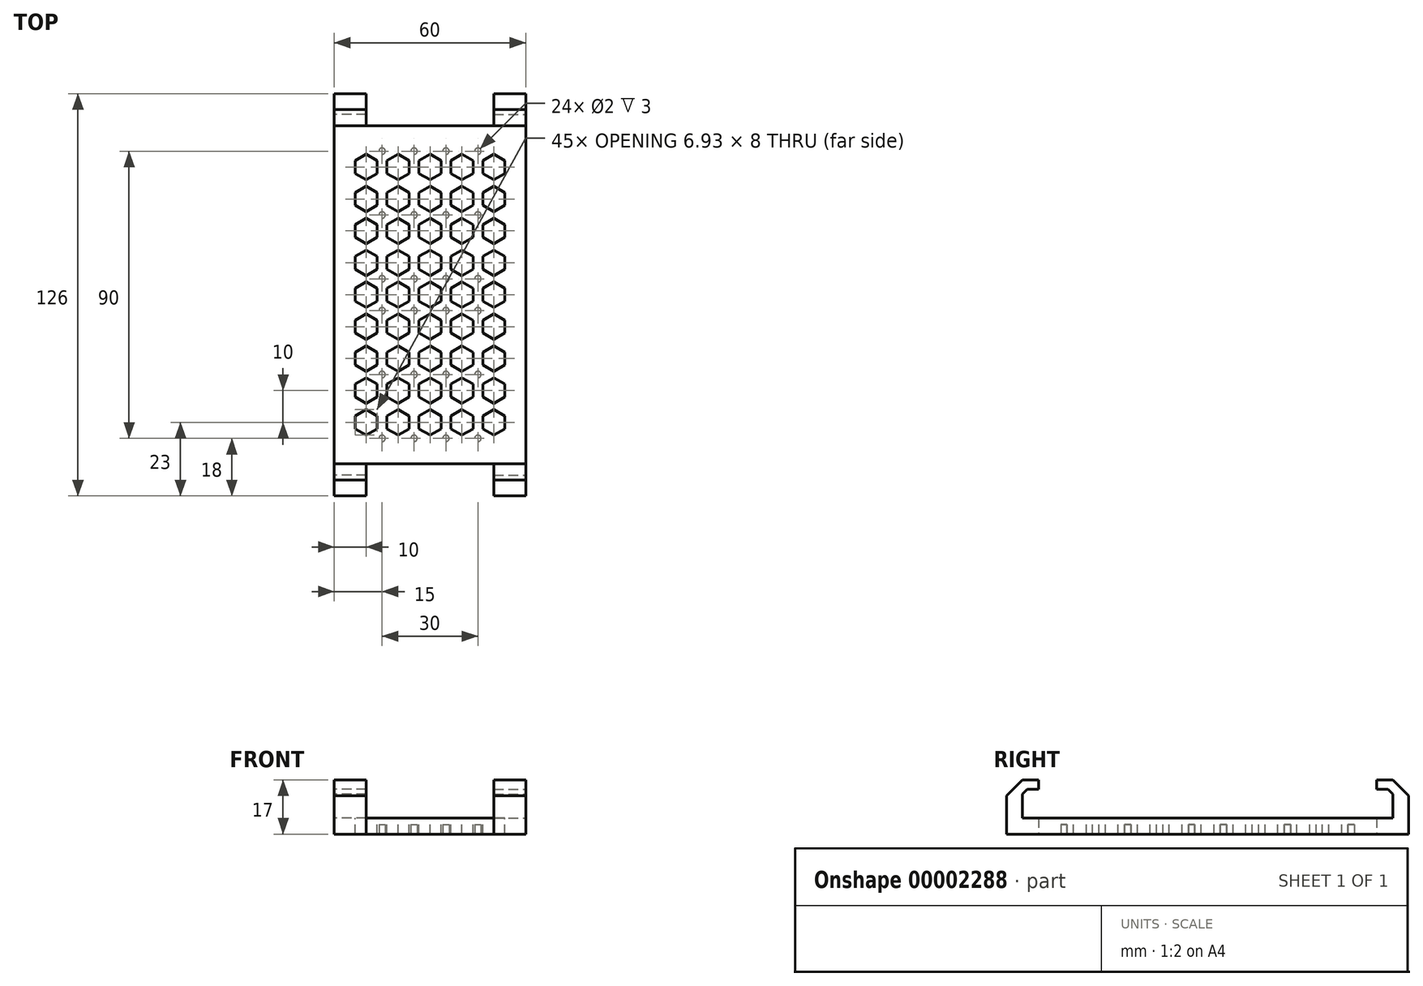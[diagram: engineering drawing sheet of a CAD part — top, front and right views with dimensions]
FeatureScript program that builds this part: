
annotation { "Feature Type Name" : "Feature", "Feature Type Description" : "" }
export const myFeature = defineFeature(function(context is Context, id is Id, definition is map)
    precondition{}
    {
        {
            var Q0;
            Q0=qCreatedBy(makeId("Top.planeOp"),FACE);
            var sketch = newSketch(context, id + "F0", { "sketchPlane" : qUnion([Q0])});
            skPoint(sketch, "E0.rect.middle", {"position": v(0, 0) * mm});
            skLineSegment(sketch, "E1", {"start": v(0, 53) * mm, "end": v(0, 0) * mm, "construction": true});
            skLineSegment(sketch, "E2.bottom", {"start": v(-30, 53) * mm, "end": v(-20, 53) * mm});
            skLineSegment(sketch, "E2.top", {"start": v(-30, 63) * mm, "end": v(-20, 63) * mm});
            skLineSegment(sketch, "E2.left", {"start": v(-30, 53) * mm, "end": v(-30, 63) * mm});
            skLineSegment(sketch, "E2.right", {"start": v(-20, 53) * mm, "end": v(-20, 63) * mm});
            skLineSegment(sketch, "E3", {"start": v(-30, 53) * mm, "end": v(-30, 0) * mm});
            skLineSegment(sketch, "E4", {"start": v(0, 0) * mm, "end": v(0, 53) * mm});
            skLineSegment(sketch, "E5", {"start": v(0, 0) * mm, "end": v(-30, 0) * mm});
            skLineSegment(sketch, "E6", {"start": v(-20, 53) * mm, "end": v(0, 53) * mm});
            skSolve(sketch);
        }
        {
            var Q0;
            Q0=qSketchRegion(id+"F0",true);
            extrude(context, id + "F1", {"entities" : qUnion([Q0]), "depth" : 5 * mm});
        }
        {
            var Q0;
            Q0=makeQuery(id+"F1.opExtrude","CAP_FACE",FACE,{"disambiguationData":[OSD([sQuery(id+"F0.wireOp",EDGE,"E0.rect.bottom"),sQuery(id+"F0.wireOp",EDGE,"E0.rect.left"),sQuery(id+"F0.wireOp",EDGE,"E0.rect.right"),sQuery(id+"F0.wireOp",EDGE,"E2.top"),sQuery(id+"F0.wireOp",EDGE,"E2.left"),sQuery(id+"F0.wireOp",EDGE,"E2.right"),sQuery(id+"F0.wireOp",EDGE,"1c330962-604c-4609-a742-9f983cd8eae2.top"),sQuery(id+"F0.wireOp",EDGE,"1c330962-604c-4609-a742-9f983cd8eae2.right"),sQuery(id+"F0.wireOp",EDGE,"8dd78533-71ad-427a-a356-95920263071d.0.MirrorCS"),sQuery(id+"F0.wireOp",EDGE,"a11a952b-e788-4085-9705-cff0ed95dc66.0.MirrorCS"),sQuery(id+"F0.wireOp",EDGE,"e45f0957-0954-452c-b698-723b5105295b.0.MirrorCS"),sQuery(id+"F0.wireOp",EDGE,"f61b77d5-9dc9-4dc6-a36b-fe702def4f4e.0.MirrorCS"),sQuery(id+"F0.wireOp",EDGE,"6235bd68-9394-4ea3-bb8d-64f7bd4e6ca2.0.MirrorCS"),sQuery(id+"F0.wireOp",EDGE,"5c020b64-50e3-4a5a-bb07-0855aa4a13f5.0.MirrorCS"),sQuery(id+"F0.wireOp",EDGE,"5c020b64-50e3-4a5a-bb07-0855aa4a13f5.1.MirrorCS"),sQuery(id+"F0.wireOp",EDGE,"5c020b64-50e3-4a5a-bb07-0855aa4a13f5.2.MirrorCS"),sQuery(id+"F0.wireOp",EDGE,"5c020b64-50e3-4a5a-bb07-0855aa4a13f5.3.MirrorCS"),sQuery(id+"F0.wireOp",EDGE,"5c020b64-50e3-4a5a-bb07-0855aa4a13f5.4.MirrorCS"),sQuery(id+"F0.wireOp",EDGE,"5c020b64-50e3-4a5a-bb07-0855aa4a13f5.6.MirrorCS"),sQuery(id+"F0.wireOp",EDGE,"5c020b64-50e3-4a5a-bb07-0855aa4a13f5.7.MirrorCS"),sQuery(id+"F0.wireOp",EDGE,"5c020b64-50e3-4a5a-bb07-0855aa4a13f5.9.MirrorCS"),sQuery(id+"F0.wireOp",EDGE,"5c020b64-50e3-4a5a-bb07-0855aa4a13f5.11.MirrorCS"),sQuery(id+"F0.wireOp",EDGE,"5c020b64-50e3-4a5a-bb07-0855aa4a13f5.12.MirrorCS"),sQuery(id+"F0.wireOp",EDGE,"5c020b64-50e3-4a5a-bb07-0855aa4a13f5.13.MirrorCS")])],"isStart":false});
            var sketch = newSketch(context, id + "F2", { "sketchPlane" : qUnion([Q0])});
            skLineSegment(sketch, "E7.bottom", {"start": v(-30, 63) * mm, "end": v(-20, 63) * mm});
            skLineSegment(sketch, "E7.top", {"start": v(-30, 53) * mm, "end": v(-20, 53) * mm});
            skLineSegment(sketch, "E7.left", {"start": v(-30, 63) * mm, "end": v(-30, 53) * mm});
            skLineSegment(sketch, "E7.right", {"start": v(-20, 63) * mm, "end": v(-20, 53) * mm});
            skSolve(sketch);
        }
        {
            var Q0;
            {var subQ3=sQuery(id+"F2.wireOp",EDGE,"E7.bottom");Q0=makeQuery(id+"F2.imprint","IMPRINT",FACE,{"disambiguationData":[TD([[makeQuery(id+"F2.imprint","IMPRINT",EDGE,{"derivedFrom":subQ3}),-1.0]])]});}
            var Q1;
            Q1=makeQuery(id+"F2.imprint","IMPRINT",FACE,{"disambiguationData":[TD([[makeQuery(id+"F2.imprint","IMPRINT",EDGE,{"derivedFrom":sQuery(id+"F2.wireOp",EDGE,"2fed119a-9cd5-4496-afa1-b7d2d9dcd837.bottom")}),1.0]])]});
            extrude(context, id + "F3", {"entities" : qUnion([Q0, Q1]), "operationType" : NewBodyOperationType.ADD, "depth" : 12 * mm});
        }
        {
            var Q0;
            Q0=makeQuery(id+"F3.boolean.opBoolean","MERGE",FACE,{"derivedFrom":[makeQuery(id+"F1.opExtrude","SWEPT_FACE",FACE,{"disambiguationData":[OSD([sQuery(id+"F0.wireOp",EDGE,"E2.left"),sQuery(id+"F0.wireOp",EDGE,"E3")])]}),makeQuery(id+"F3.opExtrude","SWEPT_FACE",FACE,{"disambiguationData":[OSD([sQuery(id+"F2.wireOp",EDGE,"E7.left")])]})]});
            var sketch = newSketch(context, id + "F4", { "sketchPlane" : qUnion([Q0])});
            skLineSegment(sketch, "E8", {"start": v(-63, 17) * mm, "end": v(-58, 17) * mm});
            skLineSegment(sketch, "E9", {"start": v(-58, 17) * mm, "end": v(-63, 12) * mm});
            skLineSegment(sketch, "E10", {"start": v(-63, 12) * mm, "end": v(-63, 17) * mm});
            skSolve(sketch);
        }
        {
            var Q0;
            Q0=qSketchRegion(id+"F4",true);
            extrude(context, id + "F5", {"entities" : qUnion([Q0]), "operationType" : NewBodyOperationType.REMOVE, "endBound" : BoundingType.THROUGH_ALL, "oppositeDirection" : true, "depth" : 25 * mm});
        }
        {
            var Q0;
            Q0=makeQuery(id+"F3.boolean.opBoolean","MERGE",FACE,{"derivedFrom":[makeQuery(id+"F1.opExtrude","SWEPT_FACE",FACE,{"disambiguationData":[OSD([sQuery(id+"F0.wireOp",EDGE,"E2.left"),sQuery(id+"F0.wireOp",EDGE,"E3")])]}),makeQuery(id+"F3.opExtrude","SWEPT_FACE",FACE,{"disambiguationData":[OSD([sQuery(id+"F2.wireOp",EDGE,"E7.left")])]})]});
            var sketch = newSketch(context, id + "F6", { "sketchPlane" : qUnion([Q0])});
            skLineSegment(sketch, "E11", {"start": v(-58, 12.5) * mm, "end": v(-58, 5) * mm});
            skLineSegment(sketch, "E12", {"start": v(-58, 5) * mm, "end": v(-53, 5) * mm});
            skLineSegment(sketch, "E13", {"start": v(-53, 5) * mm, "end": v(-53, 14) * mm});
            skLineSegment(sketch, "E14", {"start": v(-53, 14) * mm, "end": v(-56.5, 14) * mm});
            skLineSegment(sketch, "E15", {"start": v(-56.5, 14) * mm, "end": v(-58, 12.5) * mm});
            skSolve(sketch);
        }
        {
            var Q0;
            Q0=makeQuery(id+"F6.imprint","IMPRINT",FACE,{"disambiguationData":[TD([[makeQuery(id+"F6.imprint","IMPRINT",EDGE,{"derivedFrom":sQuery(id+"F6.wireOp",EDGE,"E11")}),1.0]])]});
            extrude(context, id + "F7", {"entities" : qUnion([Q0]), "operationType" : NewBodyOperationType.REMOVE, "endBound" : BoundingType.THROUGH_ALL, "oppositeDirection" : true, "depth" : 25 * mm});
        }
        {
            var Q0;
            Q0=makeQuery(id+"F1.opExtrude","SWEPT_BODY",BODY,{"disambiguationData":[OSD([sQuery(id+"F0.wireOp",EDGE,"E2.top"),sQuery(id+"F0.wireOp",EDGE,"E2.left"),sQuery(id+"F0.wireOp",EDGE,"E2.right"),sQuery(id+"F0.wireOp",EDGE,"1c330962-604c-4609-a742-9f983cd8eae2.top"),sQuery(id+"F0.wireOp",EDGE,"1c330962-604c-4609-a742-9f983cd8eae2.right"),sQuery(id+"F0.wireOp",EDGE,"5cd1e43b-32d5-4ed1-a398-68d3a370d18f.0.MirrorCS"),sQuery(id+"F0.wireOp",EDGE,"E3"),sQuery(id+"F0.wireOp",EDGE,"E4"),sQuery(id+"F0.wireOp",EDGE,"E5"),sQuery(id+"F0.wireOp",EDGE,"E6")])]});
            var Q1;
            Q1=qCreatedBy(makeId("Right.planeOp"),FACE);
            mirror(context, id + "F8", {"entities" : qUnion([Q0]), "mirrorPlane" : qUnion([Q1])});
        }
        {
            var Q0;
            Q0=makeQuery(id+"F8.opPattern","COPY",BODY,{"derivedFrom":makeQuery(id+"F1.opExtrude","SWEPT_BODY",BODY,{"disambiguationData":[OSD([sQuery(id+"F0.wireOp",EDGE,"E2.top"),sQuery(id+"F0.wireOp",EDGE,"E2.left"),sQuery(id+"F0.wireOp",EDGE,"E2.right"),sQuery(id+"F0.wireOp",EDGE,"1c330962-604c-4609-a742-9f983cd8eae2.top"),sQuery(id+"F0.wireOp",EDGE,"1c330962-604c-4609-a742-9f983cd8eae2.right"),sQuery(id+"F0.wireOp",EDGE,"5cd1e43b-32d5-4ed1-a398-68d3a370d18f.0.MirrorCS"),sQuery(id+"F0.wireOp",EDGE,"E3"),sQuery(id+"F0.wireOp",EDGE,"E4"),sQuery(id+"F0.wireOp",EDGE,"E5"),sQuery(id+"F0.wireOp",EDGE,"E6")])]}),"instanceName":"1"});
            var Q1;
            Q1=makeQuery(id+"F1.opExtrude","SWEPT_BODY",BODY,{"disambiguationData":[OSD([sQuery(id+"F0.wireOp",EDGE,"E2.top"),sQuery(id+"F0.wireOp",EDGE,"E2.left"),sQuery(id+"F0.wireOp",EDGE,"E2.right"),sQuery(id+"F0.wireOp",EDGE,"1c330962-604c-4609-a742-9f983cd8eae2.top"),sQuery(id+"F0.wireOp",EDGE,"1c330962-604c-4609-a742-9f983cd8eae2.right"),sQuery(id+"F0.wireOp",EDGE,"5cd1e43b-32d5-4ed1-a398-68d3a370d18f.0.MirrorCS"),sQuery(id+"F0.wireOp",EDGE,"E3"),sQuery(id+"F0.wireOp",EDGE,"E4"),sQuery(id+"F0.wireOp",EDGE,"E5"),sQuery(id+"F0.wireOp",EDGE,"E6")])]});
            var Q2;
            Q2=qCreatedBy(makeId("Front.planeOp"),FACE);
            mirror(context, id + "F9", {"entities" : qUnion([Q0, Q1]), "mirrorPlane" : qUnion([Q2])});
        }
        {
            var Q0;
            Q0=makeQuery(id+"F1.opExtrude","SWEPT_BODY",BODY,{"disambiguationData":[OSD([sQuery(id+"F0.wireOp",EDGE,"E2.top"),sQuery(id+"F0.wireOp",EDGE,"E2.left"),sQuery(id+"F0.wireOp",EDGE,"E2.right"),sQuery(id+"F0.wireOp",EDGE,"1c330962-604c-4609-a742-9f983cd8eae2.top"),sQuery(id+"F0.wireOp",EDGE,"1c330962-604c-4609-a742-9f983cd8eae2.right"),sQuery(id+"F0.wireOp",EDGE,"5cd1e43b-32d5-4ed1-a398-68d3a370d18f.0.MirrorCS"),sQuery(id+"F0.wireOp",EDGE,"E3"),sQuery(id+"F0.wireOp",EDGE,"E4"),sQuery(id+"F0.wireOp",EDGE,"E5"),sQuery(id+"F0.wireOp",EDGE,"E6")])]});
            var Q1;
            Q1=makeQuery(id+"F8.opPattern","COPY",BODY,{"derivedFrom":makeQuery(id+"F1.opExtrude","SWEPT_BODY",BODY,{"disambiguationData":[OSD([sQuery(id+"F0.wireOp",EDGE,"E2.top"),sQuery(id+"F0.wireOp",EDGE,"E2.left"),sQuery(id+"F0.wireOp",EDGE,"E2.right"),sQuery(id+"F0.wireOp",EDGE,"1c330962-604c-4609-a742-9f983cd8eae2.top"),sQuery(id+"F0.wireOp",EDGE,"1c330962-604c-4609-a742-9f983cd8eae2.right"),sQuery(id+"F0.wireOp",EDGE,"5cd1e43b-32d5-4ed1-a398-68d3a370d18f.0.MirrorCS"),sQuery(id+"F0.wireOp",EDGE,"E3"),sQuery(id+"F0.wireOp",EDGE,"E4"),sQuery(id+"F0.wireOp",EDGE,"E5"),sQuery(id+"F0.wireOp",EDGE,"E6")])]}),"instanceName":"1"});
            var Q2;
            Q2=makeQuery(id+"F9.opPattern","COPY",BODY,{"derivedFrom":makeQuery(id+"F1.opExtrude","SWEPT_BODY",BODY,{"disambiguationData":[OSD([sQuery(id+"F0.wireOp",EDGE,"E2.top"),sQuery(id+"F0.wireOp",EDGE,"E2.left"),sQuery(id+"F0.wireOp",EDGE,"E2.right"),sQuery(id+"F0.wireOp",EDGE,"1c330962-604c-4609-a742-9f983cd8eae2.top"),sQuery(id+"F0.wireOp",EDGE,"1c330962-604c-4609-a742-9f983cd8eae2.right"),sQuery(id+"F0.wireOp",EDGE,"5cd1e43b-32d5-4ed1-a398-68d3a370d18f.0.MirrorCS"),sQuery(id+"F0.wireOp",EDGE,"E3"),sQuery(id+"F0.wireOp",EDGE,"E4"),sQuery(id+"F0.wireOp",EDGE,"E5"),sQuery(id+"F0.wireOp",EDGE,"E6")])]}),"instanceName":"1"});
            var Q3;
            Q3=makeQuery(id+"F9.opPattern","COPY",BODY,{"derivedFrom":makeQuery(id+"F8.opPattern","COPY",BODY,{"derivedFrom":makeQuery(id+"F1.opExtrude","SWEPT_BODY",BODY,{"disambiguationData":[OSD([sQuery(id+"F0.wireOp",EDGE,"E2.top"),sQuery(id+"F0.wireOp",EDGE,"E2.left"),sQuery(id+"F0.wireOp",EDGE,"E2.right"),sQuery(id+"F0.wireOp",EDGE,"1c330962-604c-4609-a742-9f983cd8eae2.top"),sQuery(id+"F0.wireOp",EDGE,"1c330962-604c-4609-a742-9f983cd8eae2.right"),sQuery(id+"F0.wireOp",EDGE,"5cd1e43b-32d5-4ed1-a398-68d3a370d18f.0.MirrorCS"),sQuery(id+"F0.wireOp",EDGE,"E3"),sQuery(id+"F0.wireOp",EDGE,"E4"),sQuery(id+"F0.wireOp",EDGE,"E5"),sQuery(id+"F0.wireOp",EDGE,"E6")])]}),"instanceName":"1"}),"instanceName":"1"});
            booleanBodies(context, id + "F10", {"operationType" : BooleanOperationType.UNION, "tools" : qUnion([Q0, Q1, Q2, Q3])});
        }
        {
            var Q0;
            {var subQ0=sQuery(id+"F0.wireOp",EDGE,"E2.left");var subQ1=sQuery(id+"F0.wireOp",EDGE,"E2.right");var subQ2=sQuery(id+"F0.wireOp",EDGE,"5cd1e43b-32d5-4ed1-a398-68d3a370d18f.0.MirrorCS");var subQ3=sQuery(id+"F0.wireOp",EDGE,"E3");var subQ4=sQuery(id+"F0.wireOp",EDGE,"E4");var subQ5=sQuery(id+"F0.wireOp",EDGE,"E5");var subQ6=sQuery(id+"F0.wireOp",EDGE,"E6");var subQ7=makeQuery(id+"Fhmo5EDbbS1xftA_1.boolean.opBoolean","SPLIT",FACE,{"disambiguationData":[TD([makeQuery(id+"F1.opExtrude","SWEPT_FACE",FACE,{"disambiguationData":[OSD([subQ1])]})])],"derivedFrom":makeQuery(id+"F1.opExtrude","CAP_FACE",FACE,{"disambiguationData":[OSD([sQuery(id+"F0.wireOp",EDGE,"E2.top"),subQ0,subQ1,sQuery(id+"F0.wireOp",EDGE,"1c330962-604c-4609-a742-9f983cd8eae2.top"),sQuery(id+"F0.wireOp",EDGE,"1c330962-604c-4609-a742-9f983cd8eae2.right"),subQ2,subQ3,subQ4,subQ5,subQ6])],"isStart":false})});var subQ8=makeQuery(id+"F8.opPattern","COPY",FACE,{"derivedFrom":subQ7,"instanceName":"1"});Q0=makeQuery(id+"F10.opBoolean","MERGE",FACE,{"derivedFrom":[subQ7,subQ8,makeQuery(id+"F9.opPattern","COPY",FACE,{"derivedFrom":subQ7,"instanceName":"1"}),makeQuery(id+"F9.opPattern","COPY",FACE,{"derivedFrom":subQ8,"instanceName":"1"})]});}
            var sketch = newSketch(context, id + "F11", { "sketchPlane" : qUnion([Q0])});
            skCircle(sketch, "E16.cCircle", {"center": v(-20, 40) * mm, "radius": 4 * mm, "construction": true});
            skLineSegment(sketch, "E16.0", {"start": v(-16.54, 38) * mm, "end": v(-20, 36) * mm});
            skLineSegment(sketch, "E16.1", {"start": v(-20, 36) * mm, "end": v(-23.46, 38) * mm});
            skLineSegment(sketch, "E16.2", {"start": v(-23.46, 38) * mm, "end": v(-23.46, 42) * mm});
            skLineSegment(sketch, "E16.3", {"start": v(-23.46, 42) * mm, "end": v(-20, 44) * mm});
            skLineSegment(sketch, "E16.4", {"start": v(-20, 44) * mm, "end": v(-16.54, 42) * mm});
            skLineSegment(sketch, "E16.5", {"start": v(-16.54, 42) * mm, "end": v(-16.54, 38) * mm});
            skLineSegment(sketch, "E17.0.1.0", {"start": v(-23.46, 28) * mm, "end": v(-23.46, 32) * mm});
            skLineSegment(sketch, "E17.0.1.1", {"start": v(-23.46, 32) * mm, "end": v(-20, 34) * mm});
            skLineSegment(sketch, "E17.0.1.2", {"start": v(-20, 34) * mm, "end": v(-16.54, 32) * mm});
            skLineSegment(sketch, "E17.0.1.3", {"start": v(-16.54, 32) * mm, "end": v(-16.54, 28) * mm});
            skLineSegment(sketch, "E17.0.1.4", {"start": v(-16.54, 28) * mm, "end": v(-20, 26) * mm});
            skLineSegment(sketch, "E17.0.1.5", {"start": v(-20, 26) * mm, "end": v(-23.46, 28) * mm});
            skLineSegment(sketch, "E17.0.2.0", {"start": v(-23.46, 18) * mm, "end": v(-23.46, 22) * mm});
            skLineSegment(sketch, "E17.0.2.1", {"start": v(-23.46, 22) * mm, "end": v(-20, 24) * mm});
            skLineSegment(sketch, "E17.0.2.2", {"start": v(-20, 24) * mm, "end": v(-16.54, 22) * mm});
            skLineSegment(sketch, "E17.0.2.3", {"start": v(-16.54, 22) * mm, "end": v(-16.54, 18) * mm});
            skLineSegment(sketch, "E17.0.2.4", {"start": v(-16.54, 18) * mm, "end": v(-20, 16) * mm});
            skLineSegment(sketch, "E17.0.2.5", {"start": v(-20, 16) * mm, "end": v(-23.46, 18) * mm});
            skLineSegment(sketch, "E17.0.3.0", {"start": v(-23.46, 8) * mm, "end": v(-23.46, 12) * mm});
            skLineSegment(sketch, "E17.0.3.1", {"start": v(-23.46, 12) * mm, "end": v(-20, 14) * mm});
            skLineSegment(sketch, "E17.0.3.2", {"start": v(-20, 14) * mm, "end": v(-16.54, 12) * mm});
            skLineSegment(sketch, "E17.0.3.3", {"start": v(-16.54, 12) * mm, "end": v(-16.54, 8) * mm});
            skLineSegment(sketch, "E17.0.3.4", {"start": v(-16.54, 8) * mm, "end": v(-20, 6) * mm});
            skLineSegment(sketch, "E17.0.3.5", {"start": v(-20, 6) * mm, "end": v(-23.46, 8) * mm});
            skLineSegment(sketch, "E17.0.4.0", {"start": v(-23.46, -2) * mm, "end": v(-23.46, 2) * mm});
            skLineSegment(sketch, "E17.0.4.1", {"start": v(-23.46, 2) * mm, "end": v(-20, 4) * mm});
            skLineSegment(sketch, "E17.0.4.2", {"start": v(-20, 4) * mm, "end": v(-16.54, 2) * mm});
            skLineSegment(sketch, "E17.0.4.3", {"start": v(-16.54, 2) * mm, "end": v(-16.54, -2) * mm});
            skLineSegment(sketch, "E17.0.4.4", {"start": v(-16.54, -2) * mm, "end": v(-20, -4) * mm});
            skLineSegment(sketch, "E17.0.4.5", {"start": v(-20, -4) * mm, "end": v(-23.46, -2) * mm});
            skLineSegment(sketch, "E17.0.5.0", {"start": v(-23.46, -12) * mm, "end": v(-23.46, -8) * mm});
            skLineSegment(sketch, "E17.0.5.1", {"start": v(-23.46, -8) * mm, "end": v(-20, -6) * mm});
            skLineSegment(sketch, "E17.0.5.2", {"start": v(-20, -6) * mm, "end": v(-16.54, -8) * mm});
            skLineSegment(sketch, "E17.0.5.3", {"start": v(-16.54, -8) * mm, "end": v(-16.54, -12) * mm});
            skLineSegment(sketch, "E17.0.5.4", {"start": v(-16.54, -12) * mm, "end": v(-20, -14) * mm});
            skLineSegment(sketch, "E17.0.5.5", {"start": v(-20, -14) * mm, "end": v(-23.46, -12) * mm});
            skLineSegment(sketch, "E17.0.6.0", {"start": v(-23.46, -22) * mm, "end": v(-23.46, -18) * mm});
            skLineSegment(sketch, "E17.0.6.1", {"start": v(-23.46, -18) * mm, "end": v(-20, -16) * mm});
            skLineSegment(sketch, "E17.0.6.2", {"start": v(-20, -16) * mm, "end": v(-16.54, -18) * mm});
            skLineSegment(sketch, "E17.0.6.3", {"start": v(-16.54, -18) * mm, "end": v(-16.54, -22) * mm});
            skLineSegment(sketch, "E17.0.6.4", {"start": v(-16.54, -22) * mm, "end": v(-20, -24) * mm});
            skLineSegment(sketch, "E17.0.6.5", {"start": v(-20, -24) * mm, "end": v(-23.46, -22) * mm});
            skLineSegment(sketch, "E17.0.7.0", {"start": v(-23.46, -32) * mm, "end": v(-23.46, -28) * mm});
            skLineSegment(sketch, "E17.0.7.1", {"start": v(-23.46, -28) * mm, "end": v(-20, -26) * mm});
            skLineSegment(sketch, "E17.0.7.2", {"start": v(-20, -26) * mm, "end": v(-16.54, -28) * mm});
            skLineSegment(sketch, "E17.0.7.3", {"start": v(-16.54, -28) * mm, "end": v(-16.54, -32) * mm});
            skLineSegment(sketch, "E17.0.7.4", {"start": v(-16.54, -32) * mm, "end": v(-20, -34) * mm});
            skLineSegment(sketch, "E17.0.7.5", {"start": v(-20, -34) * mm, "end": v(-23.46, -32) * mm});
            skLineSegment(sketch, "E17.0.8.0", {"start": v(-23.46, -42) * mm, "end": v(-23.46, -38) * mm});
            skLineSegment(sketch, "E17.0.8.1", {"start": v(-23.46, -38) * mm, "end": v(-20, -36) * mm});
            skLineSegment(sketch, "E17.0.8.2", {"start": v(-20, -36) * mm, "end": v(-16.54, -38) * mm});
            skLineSegment(sketch, "E17.0.8.3", {"start": v(-16.54, -38) * mm, "end": v(-16.54, -42) * mm});
            skLineSegment(sketch, "E17.0.8.4", {"start": v(-16.54, -42) * mm, "end": v(-20, -44) * mm});
            skLineSegment(sketch, "E17.0.8.5", {"start": v(-20, -44) * mm, "end": v(-23.46, -42) * mm});
            skLineSegment(sketch, "E17.1.0.0", {"start": v(-13.46, 38) * mm, "end": v(-13.46, 42) * mm});
            skLineSegment(sketch, "E17.1.0.1", {"start": v(-13.46, 42) * mm, "end": v(-10, 44) * mm});
            skLineSegment(sketch, "E17.1.0.2", {"start": v(-10, 44) * mm, "end": v(-6.54, 42) * mm});
            skLineSegment(sketch, "E17.1.0.3", {"start": v(-6.54, 42) * mm, "end": v(-6.54, 38) * mm});
            skLineSegment(sketch, "E17.1.0.4", {"start": v(-6.54, 38) * mm, "end": v(-10, 36) * mm});
            skLineSegment(sketch, "E17.1.0.5", {"start": v(-10, 36) * mm, "end": v(-13.46, 38) * mm});
            skLineSegment(sketch, "E17.1.1.0", {"start": v(-13.46, 28) * mm, "end": v(-13.46, 32) * mm});
            skLineSegment(sketch, "E17.1.1.1", {"start": v(-13.46, 32) * mm, "end": v(-10, 34) * mm});
            skLineSegment(sketch, "E17.1.1.2", {"start": v(-10, 34) * mm, "end": v(-6.54, 32) * mm});
            skLineSegment(sketch, "E17.1.1.3", {"start": v(-6.54, 32) * mm, "end": v(-6.54, 28) * mm});
            skLineSegment(sketch, "E17.1.1.4", {"start": v(-6.54, 28) * mm, "end": v(-10, 26) * mm});
            skLineSegment(sketch, "E17.1.1.5", {"start": v(-10, 26) * mm, "end": v(-13.46, 28) * mm});
            skLineSegment(sketch, "E17.1.2.0", {"start": v(-13.46, 18) * mm, "end": v(-13.46, 22) * mm});
            skLineSegment(sketch, "E17.1.2.1", {"start": v(-13.46, 22) * mm, "end": v(-10, 24) * mm});
            skLineSegment(sketch, "E17.1.2.2", {"start": v(-10, 24) * mm, "end": v(-6.54, 22) * mm});
            skLineSegment(sketch, "E17.1.2.3", {"start": v(-6.54, 22) * mm, "end": v(-6.54, 18) * mm});
            skLineSegment(sketch, "E17.1.2.4", {"start": v(-6.54, 18) * mm, "end": v(-10, 16) * mm});
            skLineSegment(sketch, "E17.1.2.5", {"start": v(-10, 16) * mm, "end": v(-13.46, 18) * mm});
            skLineSegment(sketch, "E17.1.3.0", {"start": v(-13.46, 8) * mm, "end": v(-13.46, 12) * mm});
            skLineSegment(sketch, "E17.1.3.1", {"start": v(-13.46, 12) * mm, "end": v(-10, 14) * mm});
            skLineSegment(sketch, "E17.1.3.2", {"start": v(-10, 14) * mm, "end": v(-6.54, 12) * mm});
            skLineSegment(sketch, "E17.1.3.3", {"start": v(-6.54, 12) * mm, "end": v(-6.54, 8) * mm});
            skLineSegment(sketch, "E17.1.3.4", {"start": v(-6.54, 8) * mm, "end": v(-10, 6) * mm});
            skLineSegment(sketch, "E17.1.3.5", {"start": v(-10, 6) * mm, "end": v(-13.46, 8) * mm});
            skLineSegment(sketch, "E17.1.4.0", {"start": v(-13.46, -2) * mm, "end": v(-13.46, 2) * mm});
            skLineSegment(sketch, "E17.1.4.1", {"start": v(-13.46, 2) * mm, "end": v(-10, 4) * mm});
            skLineSegment(sketch, "E17.1.4.2", {"start": v(-10, 4) * mm, "end": v(-6.54, 2) * mm});
            skLineSegment(sketch, "E17.1.4.3", {"start": v(-6.54, 2) * mm, "end": v(-6.54, -2) * mm});
            skLineSegment(sketch, "E17.1.4.4", {"start": v(-6.54, -2) * mm, "end": v(-10, -4) * mm});
            skLineSegment(sketch, "E17.1.4.5", {"start": v(-10, -4) * mm, "end": v(-13.46, -2) * mm});
            skLineSegment(sketch, "E17.1.5.0", {"start": v(-13.46, -12) * mm, "end": v(-13.46, -8) * mm});
            skLineSegment(sketch, "E17.1.5.1", {"start": v(-13.46, -8) * mm, "end": v(-10, -6) * mm});
            skLineSegment(sketch, "E17.1.5.2", {"start": v(-10, -6) * mm, "end": v(-6.54, -8) * mm});
            skLineSegment(sketch, "E17.1.5.3", {"start": v(-6.54, -8) * mm, "end": v(-6.54, -12) * mm});
            skLineSegment(sketch, "E17.1.5.4", {"start": v(-6.54, -12) * mm, "end": v(-10, -14) * mm});
            skLineSegment(sketch, "E17.1.5.5", {"start": v(-10, -14) * mm, "end": v(-13.46, -12) * mm});
            skLineSegment(sketch, "E17.1.6.0", {"start": v(-13.46, -22) * mm, "end": v(-13.46, -18) * mm});
            skLineSegment(sketch, "E17.1.6.1", {"start": v(-13.46, -18) * mm, "end": v(-10, -16) * mm});
            skLineSegment(sketch, "E17.1.6.2", {"start": v(-10, -16) * mm, "end": v(-6.54, -18) * mm});
            skLineSegment(sketch, "E17.1.6.3", {"start": v(-6.54, -18) * mm, "end": v(-6.54, -22) * mm});
            skLineSegment(sketch, "E17.1.6.4", {"start": v(-6.54, -22) * mm, "end": v(-10, -24) * mm});
            skLineSegment(sketch, "E17.1.6.5", {"start": v(-10, -24) * mm, "end": v(-13.46, -22) * mm});
            skLineSegment(sketch, "E17.1.7.0", {"start": v(-13.46, -32) * mm, "end": v(-13.46, -28) * mm});
            skLineSegment(sketch, "E17.1.7.1", {"start": v(-13.46, -28) * mm, "end": v(-10, -26) * mm});
            skLineSegment(sketch, "E17.1.7.2", {"start": v(-10, -26) * mm, "end": v(-6.54, -28) * mm});
            skLineSegment(sketch, "E17.1.7.3", {"start": v(-6.54, -28) * mm, "end": v(-6.54, -32) * mm});
            skLineSegment(sketch, "E17.1.7.4", {"start": v(-6.54, -32) * mm, "end": v(-10, -34) * mm});
            skLineSegment(sketch, "E17.1.7.5", {"start": v(-10, -34) * mm, "end": v(-13.46, -32) * mm});
            skLineSegment(sketch, "E17.1.8.0", {"start": v(-13.46, -42) * mm, "end": v(-13.46, -38) * mm});
            skLineSegment(sketch, "E17.1.8.1", {"start": v(-13.46, -38) * mm, "end": v(-10, -36) * mm});
            skLineSegment(sketch, "E17.1.8.2", {"start": v(-10, -36) * mm, "end": v(-6.54, -38) * mm});
            skLineSegment(sketch, "E17.1.8.3", {"start": v(-6.54, -38) * mm, "end": v(-6.54, -42) * mm});
            skLineSegment(sketch, "E17.1.8.4", {"start": v(-6.54, -42) * mm, "end": v(-10, -44) * mm});
            skLineSegment(sketch, "E17.1.8.5", {"start": v(-10, -44) * mm, "end": v(-13.46, -42) * mm});
            skLineSegment(sketch, "E17.2.0.0", {"start": v(-3.46, 38) * mm, "end": v(-3.46, 42) * mm});
            skLineSegment(sketch, "E17.2.0.1", {"start": v(-3.46, 42) * mm, "end": v(0, 44) * mm});
            skLineSegment(sketch, "E17.2.0.2", {"start": v(0, 44) * mm, "end": v(3.46, 42) * mm});
            skLineSegment(sketch, "E17.2.0.3", {"start": v(3.46, 42) * mm, "end": v(3.46, 38) * mm});
            skLineSegment(sketch, "E17.2.0.4", {"start": v(3.46, 38) * mm, "end": v(0, 36) * mm});
            skLineSegment(sketch, "E17.2.0.5", {"start": v(0, 36) * mm, "end": v(-3.46, 38) * mm});
            skLineSegment(sketch, "E17.2.1.0", {"start": v(-3.46, 28) * mm, "end": v(-3.46, 32) * mm});
            skLineSegment(sketch, "E17.2.1.1", {"start": v(-3.46, 32) * mm, "end": v(0, 34) * mm});
            skLineSegment(sketch, "E17.2.1.2", {"start": v(0, 34) * mm, "end": v(3.46, 32) * mm});
            skLineSegment(sketch, "E17.2.1.3", {"start": v(3.46, 32) * mm, "end": v(3.46, 28) * mm});
            skLineSegment(sketch, "E17.2.1.4", {"start": v(3.46, 28) * mm, "end": v(0, 26) * mm});
            skLineSegment(sketch, "E17.2.1.5", {"start": v(0, 26) * mm, "end": v(-3.46, 28) * mm});
            skLineSegment(sketch, "E17.2.2.0", {"start": v(-3.46, 18) * mm, "end": v(-3.46, 22) * mm});
            skLineSegment(sketch, "E17.2.2.1", {"start": v(-3.46, 22) * mm, "end": v(0, 24) * mm});
            skLineSegment(sketch, "E17.2.2.2", {"start": v(0, 24) * mm, "end": v(3.46, 22) * mm});
            skLineSegment(sketch, "E17.2.2.3", {"start": v(3.46, 22) * mm, "end": v(3.46, 18) * mm});
            skLineSegment(sketch, "E17.2.2.4", {"start": v(3.46, 18) * mm, "end": v(0, 16) * mm});
            skLineSegment(sketch, "E17.2.2.5", {"start": v(0, 16) * mm, "end": v(-3.46, 18) * mm});
            skLineSegment(sketch, "E17.2.3.0", {"start": v(-3.46, 8) * mm, "end": v(-3.46, 12) * mm});
            skLineSegment(sketch, "E17.2.3.1", {"start": v(-3.46, 12) * mm, "end": v(0, 14) * mm});
            skLineSegment(sketch, "E17.2.3.2", {"start": v(0, 14) * mm, "end": v(3.46, 12) * mm});
            skLineSegment(sketch, "E17.2.3.3", {"start": v(3.46, 12) * mm, "end": v(3.46, 8) * mm});
            skLineSegment(sketch, "E17.2.3.4", {"start": v(3.46, 8) * mm, "end": v(0, 6) * mm});
            skLineSegment(sketch, "E17.2.3.5", {"start": v(0, 6) * mm, "end": v(-3.46, 8) * mm});
            skLineSegment(sketch, "E17.2.4.0", {"start": v(-3.46, -2) * mm, "end": v(-3.46, 2) * mm});
            skLineSegment(sketch, "E17.2.4.1", {"start": v(-3.46, 2) * mm, "end": v(0, 4) * mm});
            skLineSegment(sketch, "E17.2.4.2", {"start": v(0, 4) * mm, "end": v(3.46, 2) * mm});
            skLineSegment(sketch, "E17.2.4.3", {"start": v(3.46, 2) * mm, "end": v(3.46, -2) * mm});
            skLineSegment(sketch, "E17.2.4.4", {"start": v(3.46, -2) * mm, "end": v(0, -4) * mm});
            skLineSegment(sketch, "E17.2.4.5", {"start": v(0, -4) * mm, "end": v(-3.46, -2) * mm});
            skLineSegment(sketch, "E17.2.5.0", {"start": v(-3.46, -12) * mm, "end": v(-3.46, -8) * mm});
            skLineSegment(sketch, "E17.2.5.1", {"start": v(-3.46, -8) * mm, "end": v(0, -6) * mm});
            skLineSegment(sketch, "E17.2.5.2", {"start": v(0, -6) * mm, "end": v(3.46, -8) * mm});
            skLineSegment(sketch, "E17.2.5.3", {"start": v(3.46, -8) * mm, "end": v(3.46, -12) * mm});
            skLineSegment(sketch, "E17.2.5.4", {"start": v(3.46, -12) * mm, "end": v(0, -14) * mm});
            skLineSegment(sketch, "E17.2.5.5", {"start": v(0, -14) * mm, "end": v(-3.46, -12) * mm});
            skLineSegment(sketch, "E17.2.6.0", {"start": v(-3.46, -22) * mm, "end": v(-3.46, -18) * mm});
            skLineSegment(sketch, "E17.2.6.1", {"start": v(-3.46, -18) * mm, "end": v(0, -16) * mm});
            skLineSegment(sketch, "E17.2.6.2", {"start": v(0, -16) * mm, "end": v(3.46, -18) * mm});
            skLineSegment(sketch, "E17.2.6.3", {"start": v(3.46, -18) * mm, "end": v(3.46, -22) * mm});
            skLineSegment(sketch, "E17.2.6.4", {"start": v(3.46, -22) * mm, "end": v(0, -24) * mm});
            skLineSegment(sketch, "E17.2.6.5", {"start": v(0, -24) * mm, "end": v(-3.46, -22) * mm});
            skLineSegment(sketch, "E17.2.7.0", {"start": v(-3.46, -32) * mm, "end": v(-3.46, -28) * mm});
            skLineSegment(sketch, "E17.2.7.1", {"start": v(-3.46, -28) * mm, "end": v(0, -26) * mm});
            skLineSegment(sketch, "E17.2.7.2", {"start": v(0, -26) * mm, "end": v(3.46, -28) * mm});
            skLineSegment(sketch, "E17.2.7.3", {"start": v(3.46, -28) * mm, "end": v(3.46, -32) * mm});
            skLineSegment(sketch, "E17.2.7.4", {"start": v(3.46, -32) * mm, "end": v(0, -34) * mm});
            skLineSegment(sketch, "E17.2.7.5", {"start": v(0, -34) * mm, "end": v(-3.46, -32) * mm});
            skLineSegment(sketch, "E17.2.8.0", {"start": v(-3.46, -42) * mm, "end": v(-3.46, -38) * mm});
            skLineSegment(sketch, "E17.2.8.1", {"start": v(-3.46, -38) * mm, "end": v(0, -36) * mm});
            skLineSegment(sketch, "E17.2.8.2", {"start": v(0, -36) * mm, "end": v(3.46, -38) * mm});
            skLineSegment(sketch, "E17.2.8.3", {"start": v(3.46, -38) * mm, "end": v(3.46, -42) * mm});
            skLineSegment(sketch, "E17.2.8.4", {"start": v(3.46, -42) * mm, "end": v(0, -44) * mm});
            skLineSegment(sketch, "E17.2.8.5", {"start": v(0, -44) * mm, "end": v(-3.46, -42) * mm});
            skLineSegment(sketch, "E17.3.0.0", {"start": v(6.54, 38) * mm, "end": v(6.54, 42) * mm});
            skLineSegment(sketch, "E17.3.0.1", {"start": v(6.54, 42) * mm, "end": v(10, 44) * mm});
            skLineSegment(sketch, "E17.3.0.2", {"start": v(10, 44) * mm, "end": v(13.46, 42) * mm});
            skLineSegment(sketch, "E17.3.0.3", {"start": v(13.46, 42) * mm, "end": v(13.46, 38) * mm});
            skLineSegment(sketch, "E17.3.0.4", {"start": v(13.46, 38) * mm, "end": v(10, 36) * mm});
            skLineSegment(sketch, "E17.3.0.5", {"start": v(10, 36) * mm, "end": v(6.54, 38) * mm});
            skLineSegment(sketch, "E17.3.1.0", {"start": v(6.54, 28) * mm, "end": v(6.54, 32) * mm});
            skLineSegment(sketch, "E17.3.1.1", {"start": v(6.54, 32) * mm, "end": v(10, 34) * mm});
            skLineSegment(sketch, "E17.3.1.2", {"start": v(10, 34) * mm, "end": v(13.46, 32) * mm});
            skLineSegment(sketch, "E17.3.1.3", {"start": v(13.46, 32) * mm, "end": v(13.46, 28) * mm});
            skLineSegment(sketch, "E17.3.1.4", {"start": v(13.46, 28) * mm, "end": v(10, 26) * mm});
            skLineSegment(sketch, "E17.3.1.5", {"start": v(10, 26) * mm, "end": v(6.54, 28) * mm});
            skLineSegment(sketch, "E17.3.2.0", {"start": v(6.54, 18) * mm, "end": v(6.54, 22) * mm});
            skLineSegment(sketch, "E17.3.2.1", {"start": v(6.54, 22) * mm, "end": v(10, 24) * mm});
            skLineSegment(sketch, "E17.3.2.2", {"start": v(10, 24) * mm, "end": v(13.46, 22) * mm});
            skLineSegment(sketch, "E17.3.2.3", {"start": v(13.46, 22) * mm, "end": v(13.46, 18) * mm});
            skLineSegment(sketch, "E17.3.2.4", {"start": v(13.46, 18) * mm, "end": v(10, 16) * mm});
            skLineSegment(sketch, "E17.3.2.5", {"start": v(10, 16) * mm, "end": v(6.54, 18) * mm});
            skLineSegment(sketch, "E17.3.3.0", {"start": v(6.54, 8) * mm, "end": v(6.54, 12) * mm});
            skLineSegment(sketch, "E17.3.3.1", {"start": v(6.54, 12) * mm, "end": v(10, 14) * mm});
            skLineSegment(sketch, "E17.3.3.2", {"start": v(10, 14) * mm, "end": v(13.46, 12) * mm});
            skLineSegment(sketch, "E17.3.3.3", {"start": v(13.46, 12) * mm, "end": v(13.46, 8) * mm});
            skLineSegment(sketch, "E17.3.3.4", {"start": v(13.46, 8) * mm, "end": v(10, 6) * mm});
            skLineSegment(sketch, "E17.3.3.5", {"start": v(10, 6) * mm, "end": v(6.54, 8) * mm});
            skLineSegment(sketch, "E17.3.4.0", {"start": v(6.54, -2) * mm, "end": v(6.54, 2) * mm});
            skLineSegment(sketch, "E17.3.4.1", {"start": v(6.54, 2) * mm, "end": v(10, 4) * mm});
            skLineSegment(sketch, "E17.3.4.2", {"start": v(10, 4) * mm, "end": v(13.46, 2) * mm});
            skLineSegment(sketch, "E17.3.4.3", {"start": v(13.46, 2) * mm, "end": v(13.46, -2) * mm});
            skLineSegment(sketch, "E17.3.4.4", {"start": v(13.46, -2) * mm, "end": v(10, -4) * mm});
            skLineSegment(sketch, "E17.3.4.5", {"start": v(10, -4) * mm, "end": v(6.54, -2) * mm});
            skLineSegment(sketch, "E17.3.5.0", {"start": v(6.54, -12) * mm, "end": v(6.54, -8) * mm});
            skLineSegment(sketch, "E17.3.5.1", {"start": v(6.54, -8) * mm, "end": v(10, -6) * mm});
            skLineSegment(sketch, "E17.3.5.2", {"start": v(10, -6) * mm, "end": v(13.46, -8) * mm});
            skLineSegment(sketch, "E17.3.5.3", {"start": v(13.46, -8) * mm, "end": v(13.46, -12) * mm});
            skLineSegment(sketch, "E17.3.5.4", {"start": v(13.46, -12) * mm, "end": v(10, -14) * mm});
            skLineSegment(sketch, "E17.3.5.5", {"start": v(10, -14) * mm, "end": v(6.54, -12) * mm});
            skLineSegment(sketch, "E17.3.6.0", {"start": v(6.54, -22) * mm, "end": v(6.54, -18) * mm});
            skLineSegment(sketch, "E17.3.6.1", {"start": v(6.54, -18) * mm, "end": v(10, -16) * mm});
            skLineSegment(sketch, "E17.3.6.2", {"start": v(10, -16) * mm, "end": v(13.46, -18) * mm});
            skLineSegment(sketch, "E17.3.6.3", {"start": v(13.46, -18) * mm, "end": v(13.46, -22) * mm});
            skLineSegment(sketch, "E17.3.6.4", {"start": v(13.46, -22) * mm, "end": v(10, -24) * mm});
            skLineSegment(sketch, "E17.3.6.5", {"start": v(10, -24) * mm, "end": v(6.54, -22) * mm});
            skLineSegment(sketch, "E17.3.7.0", {"start": v(6.54, -32) * mm, "end": v(6.54, -28) * mm});
            skLineSegment(sketch, "E17.3.7.1", {"start": v(6.54, -28) * mm, "end": v(10, -26) * mm});
            skLineSegment(sketch, "E17.3.7.2", {"start": v(10, -26) * mm, "end": v(13.46, -28) * mm});
            skLineSegment(sketch, "E17.3.7.3", {"start": v(13.46, -28) * mm, "end": v(13.46, -32) * mm});
            skLineSegment(sketch, "E17.3.7.4", {"start": v(13.46, -32) * mm, "end": v(10, -34) * mm});
            skLineSegment(sketch, "E17.3.7.5", {"start": v(10, -34) * mm, "end": v(6.54, -32) * mm});
            skLineSegment(sketch, "E17.3.8.0", {"start": v(6.54, -42) * mm, "end": v(6.54, -38) * mm});
            skLineSegment(sketch, "E17.3.8.1", {"start": v(6.54, -38) * mm, "end": v(10, -36) * mm});
            skLineSegment(sketch, "E17.3.8.2", {"start": v(10, -36) * mm, "end": v(13.46, -38) * mm});
            skLineSegment(sketch, "E17.3.8.3", {"start": v(13.46, -38) * mm, "end": v(13.46, -42) * mm});
            skLineSegment(sketch, "E17.3.8.4", {"start": v(13.46, -42) * mm, "end": v(10, -44) * mm});
            skLineSegment(sketch, "E17.3.8.5", {"start": v(10, -44) * mm, "end": v(6.54, -42) * mm});
            skLineSegment(sketch, "E17.4.0.0", {"start": v(16.54, 38) * mm, "end": v(16.54, 42) * mm});
            skLineSegment(sketch, "E17.4.0.1", {"start": v(16.54, 42) * mm, "end": v(20, 44) * mm});
            skLineSegment(sketch, "E17.4.0.2", {"start": v(20, 44) * mm, "end": v(23.46, 42) * mm});
            skLineSegment(sketch, "E17.4.0.3", {"start": v(23.46, 42) * mm, "end": v(23.46, 38) * mm});
            skLineSegment(sketch, "E17.4.0.4", {"start": v(23.46, 38) * mm, "end": v(20, 36) * mm});
            skLineSegment(sketch, "E17.4.0.5", {"start": v(20, 36) * mm, "end": v(16.54, 38) * mm});
            skLineSegment(sketch, "E17.4.1.0", {"start": v(16.54, 28) * mm, "end": v(16.54, 32) * mm});
            skLineSegment(sketch, "E17.4.1.1", {"start": v(16.54, 32) * mm, "end": v(20, 34) * mm});
            skLineSegment(sketch, "E17.4.1.2", {"start": v(20, 34) * mm, "end": v(23.46, 32) * mm});
            skLineSegment(sketch, "E17.4.1.3", {"start": v(23.46, 32) * mm, "end": v(23.46, 28) * mm});
            skLineSegment(sketch, "E17.4.1.4", {"start": v(23.46, 28) * mm, "end": v(20, 26) * mm});
            skLineSegment(sketch, "E17.4.1.5", {"start": v(20, 26) * mm, "end": v(16.54, 28) * mm});
            skLineSegment(sketch, "E17.4.2.0", {"start": v(16.54, 18) * mm, "end": v(16.54, 22) * mm});
            skLineSegment(sketch, "E17.4.2.1", {"start": v(16.54, 22) * mm, "end": v(20, 24) * mm});
            skLineSegment(sketch, "E17.4.2.2", {"start": v(20, 24) * mm, "end": v(23.46, 22) * mm});
            skLineSegment(sketch, "E17.4.2.3", {"start": v(23.46, 22) * mm, "end": v(23.46, 18) * mm});
            skLineSegment(sketch, "E17.4.2.4", {"start": v(23.46, 18) * mm, "end": v(20, 16) * mm});
            skLineSegment(sketch, "E17.4.2.5", {"start": v(20, 16) * mm, "end": v(16.54, 18) * mm});
            skLineSegment(sketch, "E17.4.3.0", {"start": v(16.54, 8) * mm, "end": v(16.54, 12) * mm});
            skLineSegment(sketch, "E17.4.3.1", {"start": v(16.54, 12) * mm, "end": v(20, 14) * mm});
            skLineSegment(sketch, "E17.4.3.2", {"start": v(20, 14) * mm, "end": v(23.46, 12) * mm});
            skLineSegment(sketch, "E17.4.3.3", {"start": v(23.46, 12) * mm, "end": v(23.46, 8) * mm});
            skLineSegment(sketch, "E17.4.3.4", {"start": v(23.46, 8) * mm, "end": v(20, 6) * mm});
            skLineSegment(sketch, "E17.4.3.5", {"start": v(20, 6) * mm, "end": v(16.54, 8) * mm});
            skLineSegment(sketch, "E17.4.4.0", {"start": v(16.54, -2) * mm, "end": v(16.54, 2) * mm});
            skLineSegment(sketch, "E17.4.4.1", {"start": v(16.54, 2) * mm, "end": v(20, 4) * mm});
            skLineSegment(sketch, "E17.4.4.2", {"start": v(20, 4) * mm, "end": v(23.46, 2) * mm});
            skLineSegment(sketch, "E17.4.4.3", {"start": v(23.46, 2) * mm, "end": v(23.46, -2) * mm});
            skLineSegment(sketch, "E17.4.4.4", {"start": v(23.46, -2) * mm, "end": v(20, -4) * mm});
            skLineSegment(sketch, "E17.4.4.5", {"start": v(20, -4) * mm, "end": v(16.54, -2) * mm});
            skLineSegment(sketch, "E17.4.5.0", {"start": v(16.54, -12) * mm, "end": v(16.54, -8) * mm});
            skLineSegment(sketch, "E17.4.5.1", {"start": v(16.54, -8) * mm, "end": v(20, -6) * mm});
            skLineSegment(sketch, "E17.4.5.2", {"start": v(20, -6) * mm, "end": v(23.46, -8) * mm});
            skLineSegment(sketch, "E17.4.5.3", {"start": v(23.46, -8) * mm, "end": v(23.46, -12) * mm});
            skLineSegment(sketch, "E17.4.5.4", {"start": v(23.46, -12) * mm, "end": v(20, -14) * mm});
            skLineSegment(sketch, "E17.4.5.5", {"start": v(20, -14) * mm, "end": v(16.54, -12) * mm});
            skLineSegment(sketch, "E17.4.6.0", {"start": v(16.54, -22) * mm, "end": v(16.54, -18) * mm});
            skLineSegment(sketch, "E17.4.6.1", {"start": v(16.54, -18) * mm, "end": v(20, -16) * mm});
            skLineSegment(sketch, "E17.4.6.2", {"start": v(20, -16) * mm, "end": v(23.46, -18) * mm});
            skLineSegment(sketch, "E17.4.6.3", {"start": v(23.46, -18) * mm, "end": v(23.46, -22) * mm});
            skLineSegment(sketch, "E17.4.6.4", {"start": v(23.46, -22) * mm, "end": v(20, -24) * mm});
            skLineSegment(sketch, "E17.4.6.5", {"start": v(20, -24) * mm, "end": v(16.54, -22) * mm});
            skLineSegment(sketch, "E17.4.7.0", {"start": v(16.54, -32) * mm, "end": v(16.54, -28) * mm});
            skLineSegment(sketch, "E17.4.7.1", {"start": v(16.54, -28) * mm, "end": v(20, -26) * mm});
            skLineSegment(sketch, "E17.4.7.2", {"start": v(20, -26) * mm, "end": v(23.46, -28) * mm});
            skLineSegment(sketch, "E17.4.7.3", {"start": v(23.46, -28) * mm, "end": v(23.46, -32) * mm});
            skLineSegment(sketch, "E17.4.7.4", {"start": v(23.46, -32) * mm, "end": v(20, -34) * mm});
            skLineSegment(sketch, "E17.4.7.5", {"start": v(20, -34) * mm, "end": v(16.54, -32) * mm});
            skLineSegment(sketch, "E17.4.8.0", {"start": v(16.54, -42) * mm, "end": v(16.54, -38) * mm});
            skLineSegment(sketch, "E17.4.8.1", {"start": v(16.54, -38) * mm, "end": v(20, -36) * mm});
            skLineSegment(sketch, "E17.4.8.2", {"start": v(20, -36) * mm, "end": v(23.46, -38) * mm});
            skLineSegment(sketch, "E17.4.8.3", {"start": v(23.46, -38) * mm, "end": v(23.46, -42) * mm});
            skLineSegment(sketch, "E17.4.8.4", {"start": v(23.46, -42) * mm, "end": v(20, -44) * mm});
            skLineSegment(sketch, "E17.4.8.5", {"start": v(20, -44) * mm, "end": v(16.54, -42) * mm});
            skLineSegment(sketch, "E17.direction1", {"start": v(-20, 36) * mm, "end": v(-10, 36) * mm, "construction": true});
            skLineSegment(sketch, "E17.direction2", {"start": v(-20, 36) * mm, "end": v(-20, 26) * mm, "construction": true});
            skSolve(sketch);
        }
        {
            var Q0;
            Q0=qSketchRegion(id+"F11",true);
            extrude(context, id + "F12", {"entities" : qUnion([Q0]), "operationType" : NewBodyOperationType.REMOVE, "endBound" : BoundingType.UP_TO_NEXT, "oppositeDirection" : true, "depth" : 25 * mm});
        }
        {
            var Q0;
            {var subQ0=sQuery(id+"F0.wireOp",EDGE,"E2.left");var subQ1=sQuery(id+"F0.wireOp",EDGE,"1c330962-604c-4609-a742-9f983cd8eae2.top");var subQ2=sQuery(id+"F0.wireOp",EDGE,"1c330962-604c-4609-a742-9f983cd8eae2.right");var subQ3=sQuery(id+"F0.wireOp",EDGE,"5cd1e43b-32d5-4ed1-a398-68d3a370d18f.0.MirrorCS");var subQ4=sQuery(id+"F0.wireOp",EDGE,"E3");var subQ5=sQuery(id+"F0.wireOp",EDGE,"E4");var subQ6=sQuery(id+"F0.wireOp",EDGE,"E5");var subQ7=sQuery(id+"F0.wireOp",EDGE,"E6");var subQ8=makeQuery(id+"Fa2va6a4ca5KiLj_1.boolean.opBoolean","SPLIT",FACE,{"disambiguationData":[TD([makeQuery(id+"F1.opExtrude","SWEPT_FACE",FACE,{"disambiguationData":[OSD([subQ1])]})])],"derivedFrom":makeQuery(id+"F1.opExtrude","CAP_FACE",FACE,{"disambiguationData":[OSD([sQuery(id+"F0.wireOp",EDGE,"E2.top"),subQ0,sQuery(id+"F0.wireOp",EDGE,"E2.right"),subQ1,subQ2,subQ3,subQ4,subQ5,subQ6,subQ7])],"isStart":true})});var subQ9=makeQuery(id+"F8.opPattern","COPY",FACE,{"derivedFrom":subQ8,"instanceName":"1"});Q0=makeQuery(id+"F10.opBoolean","MERGE",FACE,{"derivedFrom":[subQ8,subQ9,makeQuery(id+"F9.opPattern","COPY",FACE,{"derivedFrom":subQ8,"instanceName":"1"}),makeQuery(id+"F9.opPattern","COPY",FACE,{"derivedFrom":subQ9,"instanceName":"1"})]});}
            var sketch = newSketch(context, id + "F13", { "sketchPlane" : qUnion([Q0])});
            skCircle(sketch, "E18", {"center": v(-15, 45) * mm, "radius": 1 * mm});
            skLineSegment(sketch, "E19", {"start": v(-30, 0) * mm, "end": v(30, 0) * mm, "construction": true});
            skCircle(sketch, "E20.0.1.0", {"center": v(-15, 25) * mm, "radius": 1 * mm});
            skCircle(sketch, "E20.0.2.0", {"center": v(-15, 5) * mm, "radius": 1 * mm});
            skCircle(sketch, "E20.1.0.0", {"center": v(-5, 45) * mm, "radius": 1 * mm});
            skCircle(sketch, "E20.1.1.0", {"center": v(-5, 25) * mm, "radius": 1 * mm});
            skCircle(sketch, "E20.1.2.0", {"center": v(-5, 5) * mm, "radius": 1 * mm});
            skCircle(sketch, "E20.2.0.0", {"center": v(5, 45) * mm, "radius": 1 * mm});
            skCircle(sketch, "E20.2.1.0", {"center": v(5, 25) * mm, "radius": 1 * mm});
            skCircle(sketch, "E20.2.2.0", {"center": v(5, 5) * mm, "radius": 1 * mm});
            skCircle(sketch, "E20.3.0.0", {"center": v(15, 45) * mm, "radius": 1 * mm});
            skCircle(sketch, "E20.3.1.0", {"center": v(15, 25) * mm, "radius": 1 * mm});
            skCircle(sketch, "E20.3.2.0", {"center": v(15, 5) * mm, "radius": 1 * mm});
            skLineSegment(sketch, "E20.direction1", {"start": v(-15, 45) * mm, "end": v(-5, 45) * mm, "construction": true});
            skLineSegment(sketch, "E20.direction2", {"start": v(-15, 45) * mm, "end": v(-15, 25) * mm, "construction": true});
            skCircle(sketch, "E21.0.MirrorC", {"center": v(-5, -25) * mm, "radius": 1 * mm});
            skCircle(sketch, "E21.1.MirrorC", {"center": v(-15, -45) * mm, "radius": 1 * mm});
            skCircle(sketch, "E21.2.MirrorC", {"center": v(5, -45) * mm, "radius": 1 * mm});
            skCircle(sketch, "E21.3.MirrorC", {"center": v(-5, -45) * mm, "radius": 1 * mm});
            skLineSegment(sketch, "E21.4.MirrorCS", {"start": v(-15, -45) * mm, "end": v(-5, -45) * mm, "construction": true});
            skLineSegment(sketch, "E21.5.MirrorCS", {"start": v(-15, -45) * mm, "end": v(-15, -25) * mm, "construction": true});
            skCircle(sketch, "E21.6.MirrorC", {"center": v(5, -25) * mm, "radius": 1 * mm});
            skCircle(sketch, "E21.7.MirrorC", {"center": v(15, -25) * mm, "radius": 1 * mm});
            skCircle(sketch, "E21.8.MirrorC", {"center": v(15, -45) * mm, "radius": 1 * mm});
            skCircle(sketch, "E21.9.MirrorC", {"center": v(-15, -25) * mm, "radius": 1 * mm});
            skCircle(sketch, "E22.0.MirrorC", {"center": v(-15, -5) * mm, "radius": 1 * mm});
            skCircle(sketch, "E22.1.MirrorC", {"center": v(-5, -5) * mm, "radius": 1 * mm});
            skCircle(sketch, "E22.2.MirrorC", {"center": v(15, -5) * mm, "radius": 1 * mm});
            skCircle(sketch, "E22.3.MirrorC", {"center": v(5, -5) * mm, "radius": 1 * mm});
            skSolve(sketch);
        }
        {
            var Q0;
            Q0=qSketchRegion(id+"F13",true);
            extrude(context, id + "F14", {"entities" : qUnion([Q0]), "operationType" : NewBodyOperationType.REMOVE, "oppositeDirection" : true, "depth" : 3 * mm});
        }
    });
